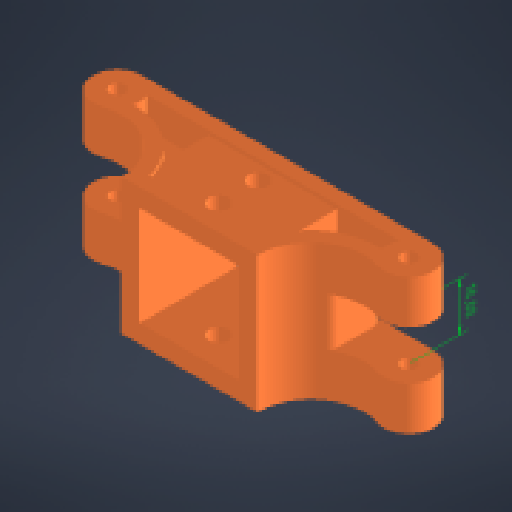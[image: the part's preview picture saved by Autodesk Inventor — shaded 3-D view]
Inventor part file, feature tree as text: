
AUTODESK INVENTOR PART (.ipt)
format: ipt  version: 2024 (Build 280153000, 153)  size: 322,048 bytes
history: native  units: mm
features: other x8, extrude x4, sketch x4, mirror x1, shell x1, fillet x1
ambient origin geometry x8: Origin, YZ Plane, XZ Plane, XY Plane, X Axis, Y Axis, Z Axis, Center Point
bodies: Body1 (feature_tree)
feature tree (19):
  other  "Твердое тело1"
  other  "Аннотации"
  extrude  "Выдавливание1"  Depth=3.0mm
  extrude  "Выдавливание2"  Depth=28.0mm
  other  "РабПлоскость2"
  extrude  "Выдавливание4"  Depth=11.0mm
  mirror  "Зеркальное отражение1"
  other  "Непосредственное редактирование2"
  shell  "Оболочка3"  Thickness=5.0mm
  extrude  "Выдавливание5"  Depth=60.0mm
  fillet  "Сопряжение1"  Radius=28.0mm
  sketch  "Эскиз1"
  sketch  "Эскиз2"
  other  "РабПлоскость1"
  sketch  "Эскиз4"
  sketch  "Эскиз5"
  other  "Перенос3"
  other  "Перенос4"
  other  "Линейный размер 1"
